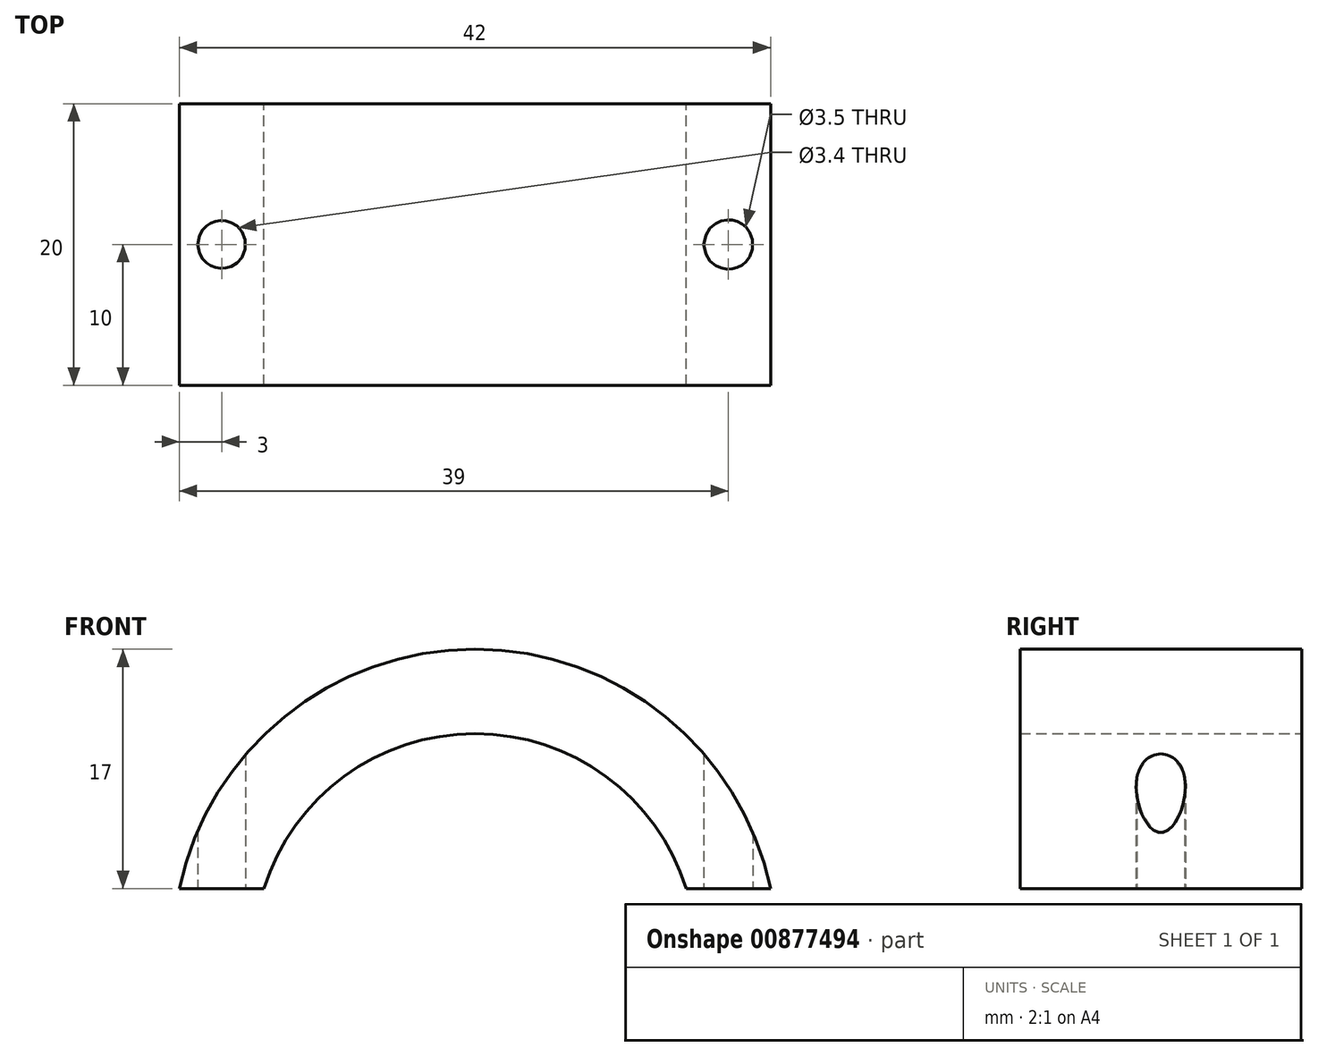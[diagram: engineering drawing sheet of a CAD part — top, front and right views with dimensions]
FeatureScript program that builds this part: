
annotation { "Feature Type Name" : "Feature", "Feature Type Description" : "" }
export const myFeature = defineFeature(function(context is Context, id is Id, definition is map)
    precondition{}
    {
        {
            var Q0;
            Q0=qCreatedBy(makeId("Front.planeOp"),FACE);
            var sketch = newSketch(context, id + "F0", { "sketchPlane" : qUnion([Q0])});
            skArc(sketch, "E0", {"start": v(15, 0) * mm, "mid": v(0, 11) * mm, "end": v(-15, 0) * mm});
            skArc(sketch, "E1", {"start": v(21, 0) * mm, "mid": v(0, 17) * mm, "end": v(-21, 0) * mm});
            skLineSegment(sketch, "E2", {"start": v(-21, 0) * mm, "end": v(-15, 0) * mm});
            skLineSegment(sketch, "E3", {"start": v(15, 0) * mm, "end": v(21, 0) * mm});
            skSolve(sketch);
        }
        {
            var Q0;
            Q0=makeQuery(id+"F0.imprint","IMPRINT",FACE,{"disambiguationData":[TD([[makeQuery(id+"F0.imprint","IMPRINT",EDGE,{"derivedFrom":sQuery(id+"F0.wireOp",EDGE,"E0")}),-1.0]])]});
            extrude(context, id + "F1", {"entities" : qUnion([Q0]), "depth" : 20 * mm, "offsetDistance" : 25 * mm});
        }
        {
            var Q0;
            Q0=makeQuery(id+"F1.opExtrude","SWEPT_FACE",FACE,{"disambiguationData":[OSD([sQuery(id+"F0.wireOp",EDGE,"E2")])]});
            var sketch = newSketch(context, id + "F2", { "sketchPlane" : qUnion([Q0])});
            skCircle(sketch, "E4", {"center": v(-18, 10) * mm, "radius": 1.7 * mm});
            skPoint(sketch, "E4.centerSnap0", {"position": v(-18, 20) * mm});
            skPoint(sketch, "E4.centerSnap1", {"position": v(-15, 10) * mm});
            skSolve(sketch);
        }
        {
            var Q0;
            Q0=makeQuery(id+"F1.opExtrude","SWEPT_FACE",FACE,{"disambiguationData":[OSD([sQuery(id+"F0.wireOp",EDGE,"E3")])]});
            var sketch = newSketch(context, id + "F3", { "sketchPlane" : qUnion([Q0])});
            skCircle(sketch, "E5", {"center": v(18, 10) * mm, "radius": 1.75 * mm});
            skPoint(sketch, "E5.centerSnap0", {"position": v(18, 0) * mm});
            skPoint(sketch, "E5.centerSnap1", {"position": v(21, 10) * mm});
            skSolve(sketch);
        }
        {
            var Q0;
            Q0=makeQuery(id+"F2.imprint","IMPRINT",FACE,{"disambiguationData":[TD([[makeQuery(id+"F2.imprint","IMPRINT",EDGE,{"derivedFrom":sQuery(id+"F2.wireOp",EDGE,"E4")}),1.0]])]});
            var Q1;
            Q1=makeQuery(id+"F3.imprint","IMPRINT",FACE,{"disambiguationData":[TD([[makeQuery(id+"F3.imprint","IMPRINT",EDGE,{"derivedFrom":sQuery(id+"F3.wireOp",EDGE,"E5")}),1.0]])]});
            extrude(context, id + "F4", {"entities" : qUnion([Q0, Q1]), "operationType" : NewBodyOperationType.REMOVE, "endBound" : BoundingType.THROUGH_ALL, "oppositeDirection" : true, "depth" : 25 * mm, "offsetDistance" : 25 * mm});
        }
    });
